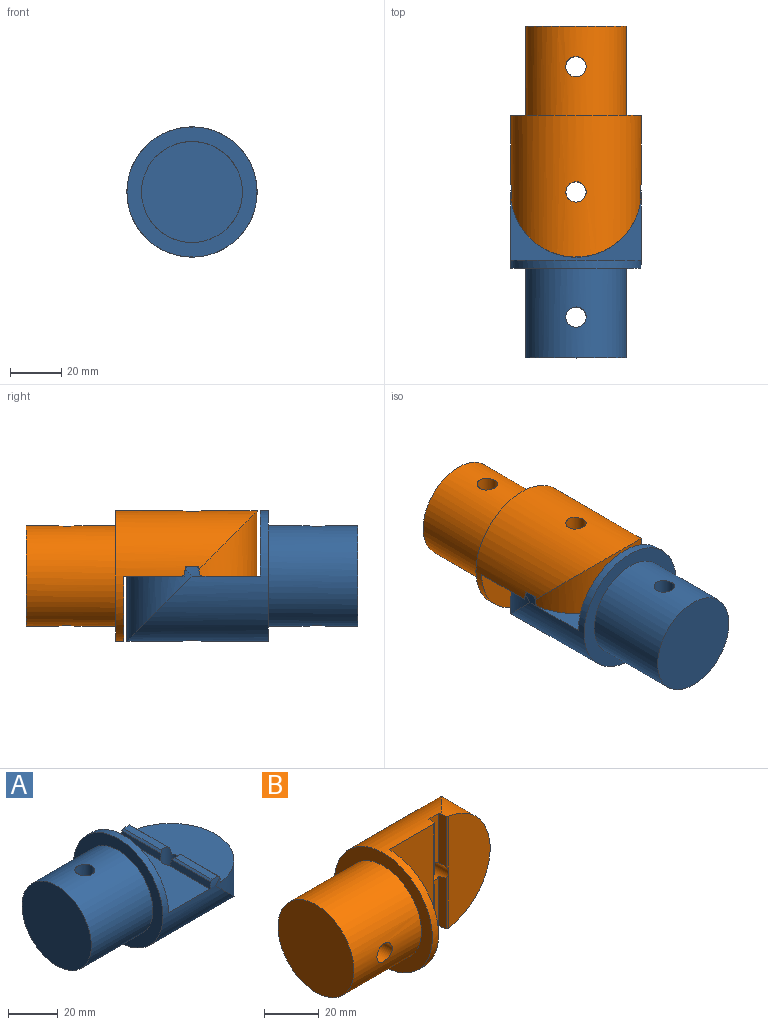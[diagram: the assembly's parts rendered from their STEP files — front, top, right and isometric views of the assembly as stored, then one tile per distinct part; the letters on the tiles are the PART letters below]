
ASSEMBLY  parts=2 mates=1
PART A: 21 faces, bbox 90.3x50.8x50.9 mm
  f0: plane 22.8x3.06mm, normal (0.98,0,0.17), area 69.8mm2, adj f2,f6,f9,f18,f20
  f1: cylinder r=25.4mm len=55.33mm, axis (-1,0,0), area 3892mm2, adj f2,f4,f5,f8,f10,f11,f12,f14
  f2: cylinder r=25.4mm len=5.76mm, axis (-1,0,0), area 16.5mm2, adj f0,f1,f3,f6,f15,f16,f18
  f3: plane 22.94x3.06mm, normal (-0.98,0,0.17), area 70.1mm2, adj f2,f14,f16,f20
  f4: plane 21.52x3.36mm, normal (0,0,1), area 71.4mm2, adj f1,f5,f17,f20
  f5: plane 22.22x0.93mm, normal (-0.64,0,0.77), area 25.5mm2, adj f1,f4,f10,f20
  f6: plane 22.22x0.93mm, normal (0.64,0,0.77), area 25.5mm2, adj f0,f2,f15,f20
  f7: cylinder r=19.69mm len=39.37mm, axis (1,0,0), area 4220mm2, adj f12,f13,f19
  f8: plane 22.8x3.06mm, normal (0.98,0,0.17), area 69.8mm2, adj f1,f9,f17,f18,f20
  f9: plane 50.42x22.29mm, normal (0,0,1), area 852.9mm2, adj f0,f8,f18,f20
  f10: plane 22.94x3.06mm, normal (-0.98,0,0.17), area 70.1mm2, adj f1,f5,f14,f20
  f11: plane 50.8x25.4mm, normal (1,0,0), area 1013.4mm2, adj f1,f14
  f12: plane 50.8x50.8mm, normal (-1,0,0), area 809.5mm2, adj f1,f7
  f13: plane 39.37x39.37mm, normal (-1,0,0), area 1217.4mm2, adj f7
  f14: plane 50.8x23.56mm, normal (0,0,1), area 1193.9mm2, adj f1,f3,f10,f11,f20
  f15: plane 21.52x3.36mm, normal (0,0,1), area 71.4mm2, adj f2,f6,f16,f20
  f16: plane 22.22x0.93mm, normal (-0.64,0,0.77), area 25.5mm2, adj f2,f3,f15,f20
  f17: plane 22.22x0.93mm, normal (0.64,0,0.77), area 25.5mm2, adj f1,f4,f8,f20
  f18: cylinder r=25.4mm len=50.8mm, axis (0,0,1), area 1298.6mm2, adj f0,f1,f2,f8,f9
  f19: cylinder r=3.97mm len=39.37mm, axis (0,0,1), area 971.7mm2, adj f7
  f20: cylinder r=3.97mm len=29.21mm, axis (0,0,1), area 675.2mm2, adj f0,f1,f3,f4,f5,f6,f8,f9
PART B: 20 faces, bbox 90.3x50.9x50.9 mm
  f0: cylinder r=19.69mm len=39.37mm, axis (1,0,0), area 4220.3mm2, adj f7,f8,f19
  f1: cylinder r=25.4mm len=55.28mm, axis (-1,0,0), area 3845.3mm2, adj f3,f4,f5,f6,f7,f9,f10,f11
  f2: plane 50.33x21.75mm, normal (0,-1,0), area 828.7mm2, adj f6,f14,f15,f16
  f3: plane 22.79x3.31mm, normal (-0.98,-0.17,0), area 75.4mm2, adj f1,f6,f11,f14,f16
  f4: plane 22.79x3.31mm, normal (-0.98,-0.17,0), area 75.4mm2, adj f1,f6,f12,f14,f15
  f5: plane 50.8x22.99mm, normal (0,-1,0), area 1167.2mm2, adj f1,f6,f9,f17,f18
  f6: cylinder r=3.97mm len=25.4mm, axis (0,-1,0), area 580.1mm2, adj f1,f2,f3,f4,f5,f10,f11,f12
  f7: plane 50.8x50.8mm, normal (-1,0,0), area 809.5mm2, adj f0,f1
  f8: plane 39.37x39.37mm, normal (-1,0,0), area 1217.4mm2, adj f0
  f9: plane 50.8x25.4mm, normal (1,0,0), area 1013.4mm2, adj f1,f5
  f10: plane 22.9x3.31mm, normal (0.98,-0.17,0), area 75.6mm2, adj f1,f6,f11,f18
  f11: plane 22.03x5.01mm, normal (0,-1,0), area 107.3mm2, adj f1,f3,f6,f10
  f12: plane 22.03x5.01mm, normal (0,-1,0), area 107.3mm2, adj f1,f4,f6,f13
  f13: plane 22.9x3.31mm, normal (0.98,-0.17,0), area 75.6mm2, adj f1,f6,f12,f17
  f14: cylinder r=25.43mm len=50.57mm, axis (0,-1,0), area 1279.8mm2, adj f1,f2,f3,f4,f15,f16
  f15: plane 23.83x0.66mm, normal (-0.64,-0.77,0), area 18mm2, adj f2,f4,f6,f14
  f16: plane 23.83x0.66mm, normal (-0.64,-0.77,0), area 18mm2, adj f2,f3,f6,f14
  f17: plane 23.98x0.66mm, normal (0.64,-0.77,0), area 18.2mm2, adj f1,f5,f6,f13
  f18: plane 23.98x0.66mm, normal (0.64,-0.77,0), area 18.2mm2, adj f1,f5,f6,f10
  f19: cylinder r=3.97mm len=39.37mm, axis (0,-1,0), area 971.7mm2, adj f0
PLACE A rot(axis=(0,0,1),90deg) t=(19.12,-66.04,-25.3)mm
PLACE B rot(axis=(0.58,-0.58,-0.58),120deg) t=(19.12,-6.35,-25.3)mm
MATE revolute A.f18 <-> B.f6  axis (0,0,1) through (19.12,-36.2,-21.49)mm
